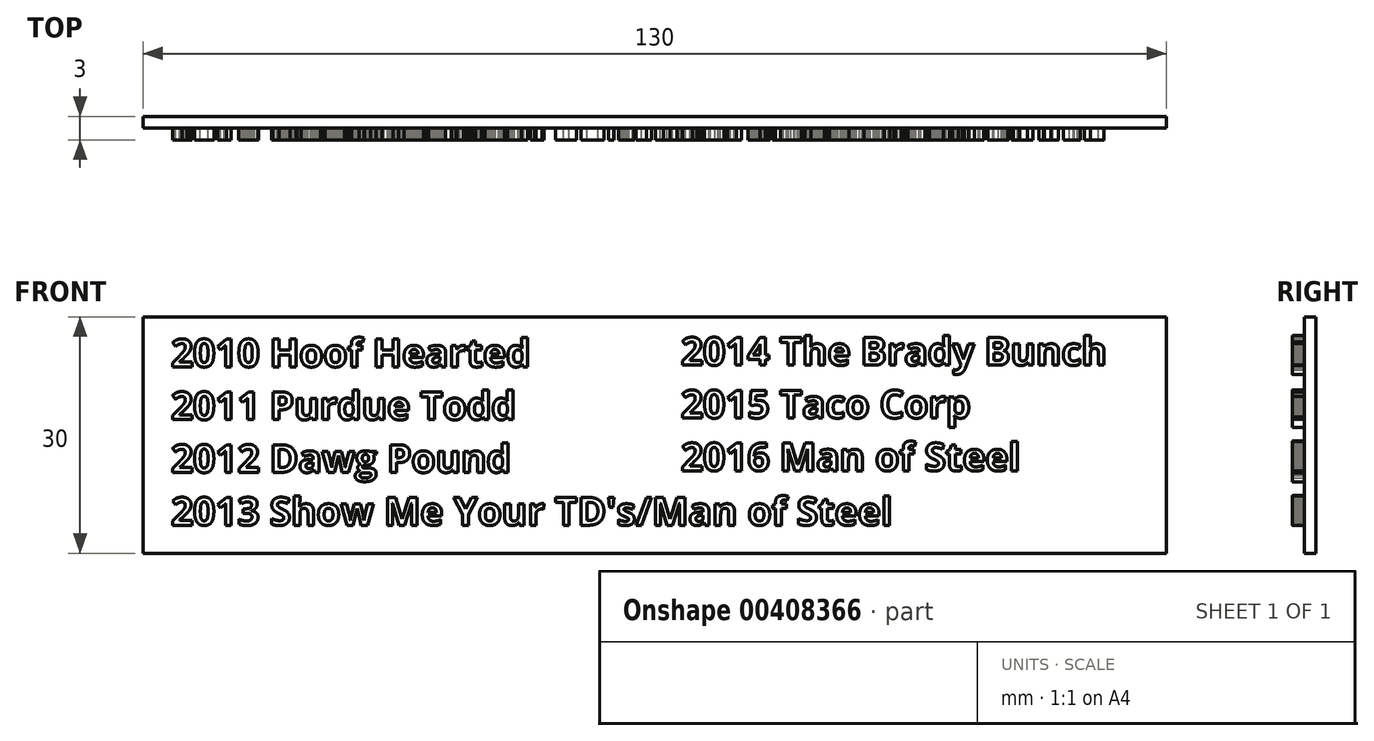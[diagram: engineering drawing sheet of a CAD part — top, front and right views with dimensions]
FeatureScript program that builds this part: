
annotation { "Feature Type Name" : "Feature", "Feature Type Description" : "" }
export const myFeature = defineFeature(function(context is Context, id is Id, definition is map)
    precondition{}
    {
        {
            var Q0;
            Q0=qCreatedBy(makeId("Front.planeOp"),FACE);
            var sketch = newSketch(context, id + "F0", { "sketchPlane" : qUnion([Q0])});
            skLineSegment(sketch, "E0", {"start": v(0, 0) * mm, "end": v(65, 0) * mm});
            skLineSegment(sketch, "E1", {"start": v(65, 0) * mm, "end": v(65, 30) * mm});
            skLineSegment(sketch, "E2", {"start": v(65, 30) * mm, "end": v(0, 30) * mm});
            skLineSegment(sketch, "E3", {"start": v(0, 30) * mm, "end": v(0, 0) * mm});
            skLineSegment(sketch, "E4.MirrorCS", {"start": v(-65, 30) * mm, "end": v(0, 30) * mm});
            skLineSegment(sketch, "E5.MirrorCS", {"start": v(-65, 0) * mm, "end": v(-65, 30) * mm});
            skLineSegment(sketch, "E6.MirrorCS", {"start": v(0, 0) * mm, "end": v(-65, 0) * mm});
            skSolve(sketch);
        }
        {
            var Q0;
            Q0=makeQuery(id+"F0.imprint","IMPRINT",FACE,{"disambiguationData":[TD([[makeQuery(id+"F0.imprint","IMPRINT",EDGE,{"derivedFrom":sQuery(id+"F0.wireOp",EDGE,"E0")}),1.0]])]});
            var Q1;
            Q1=makeQuery(id+"F0.imprint","IMPRINT",FACE,{"disambiguationData":[TD([[makeQuery(id+"F0.imprint","IMPRINT",EDGE,{"derivedFrom":sQuery(id+"F0.wireOp",EDGE,"E3")}),-1.0]])]});
            extrude(context, id + "F1", {"entities" : qUnion([Q0, Q1]), "depth" : 1.5 * mm});
        }
        {
            var Q0;
            Q0=makeQuery(id+"F1.opExtrude","CAP_FACE",FACE,{"disambiguationData":[OSD([sQuery(id+"F0.wireOp",EDGE,"E0"),sQuery(id+"F0.wireOp",EDGE,"E1"),sQuery(id+"F0.wireOp",EDGE,"E2"),sQuery(id+"F0.wireOp",EDGE,"E4.MirrorCS"),sQuery(id+"F0.wireOp",EDGE,"E5.MirrorCS"),sQuery(id+"F0.wireOp",EDGE,"E6.MirrorCS")])],"isStart":false});
            var sketch = newSketch(context, id + "F2", { "sketchPlane" : qUnion([Q0])});
            skText(sketch, "E7", { "text": "2014 The Brady Bunch\n2015 Taco Corp\n2016 Man of Steel\n", "fontName": "OpenSans-Bold.ttf"});
            const initialGuessF2  = {"E7": [0.00332, 0.02388, 1, 0, 0.00355]};
            skSetInitialGuess(sketch, initialGuessF2);
            skSolve(sketch);
        }
        {
            var Q0;
            Q0=qSketchRegion(id+"F2",true);
            extrude(context, id + "F3", {"entities" : qUnion([Q0]), "operationType" : NewBodyOperationType.ADD, "depth" : 1.5 * mm});
        }
        {
            var Q0;
            {var subQ0=sQuery(id+"F0.wireOp",EDGE,"E6.MirrorCS");var subQ1=sQuery(id+"F0.wireOp",EDGE,"E0");var subQ2=sQuery(id+"F0.wireOp",EDGE,"E1");var subQ3=sQuery(id+"F0.wireOp",EDGE,"E5.MirrorCS");var subQ4=sQuery(id+"F0.wireOp",EDGE,"E4.MirrorCS");var subQ5=sQuery(id+"F0.wireOp",EDGE,"E2");Q0=makeQuery(id+"F3.boolean.opBoolean","SPLIT",FACE,{"disambiguationData":[TD([makeQuery(id+"F1.opExtrude","SWEPT_FACE",FACE,{"disambiguationData":[OSD([subQ2])]})])],"derivedFrom":makeQuery(id+"F1.opExtrude","CAP_FACE",FACE,{"disambiguationData":[OSD([subQ1,subQ2,subQ5,subQ4,subQ3,subQ0])],"isStart":false})});}
            var sketch = newSketch(context, id + "F4", { "sketchPlane" : qUnion([Q0])});
            skText(sketch, "E8", { "text": "2010 Hoof Hearted\n2011 Purdue Todd\n2012 Dawg Pound\n2013 Show Me Your TD\'s/Man of Steel\n", "fontName": "OpenSans-Bold.ttf"});
            const initialGuessF4  = {"E8": [-0.06146, 0.02367, 1, 0, 0.00355]};
            skSetInitialGuess(sketch, initialGuessF4);
            skSolve(sketch);
        }
        {
            var Q0;
            Q0=qSketchRegion(id+"F4",true);
            extrude(context, id + "F5", {"entities" : qUnion([Q0]), "operationType" : NewBodyOperationType.ADD, "depth" : 1.5 * mm});
        }
    });
